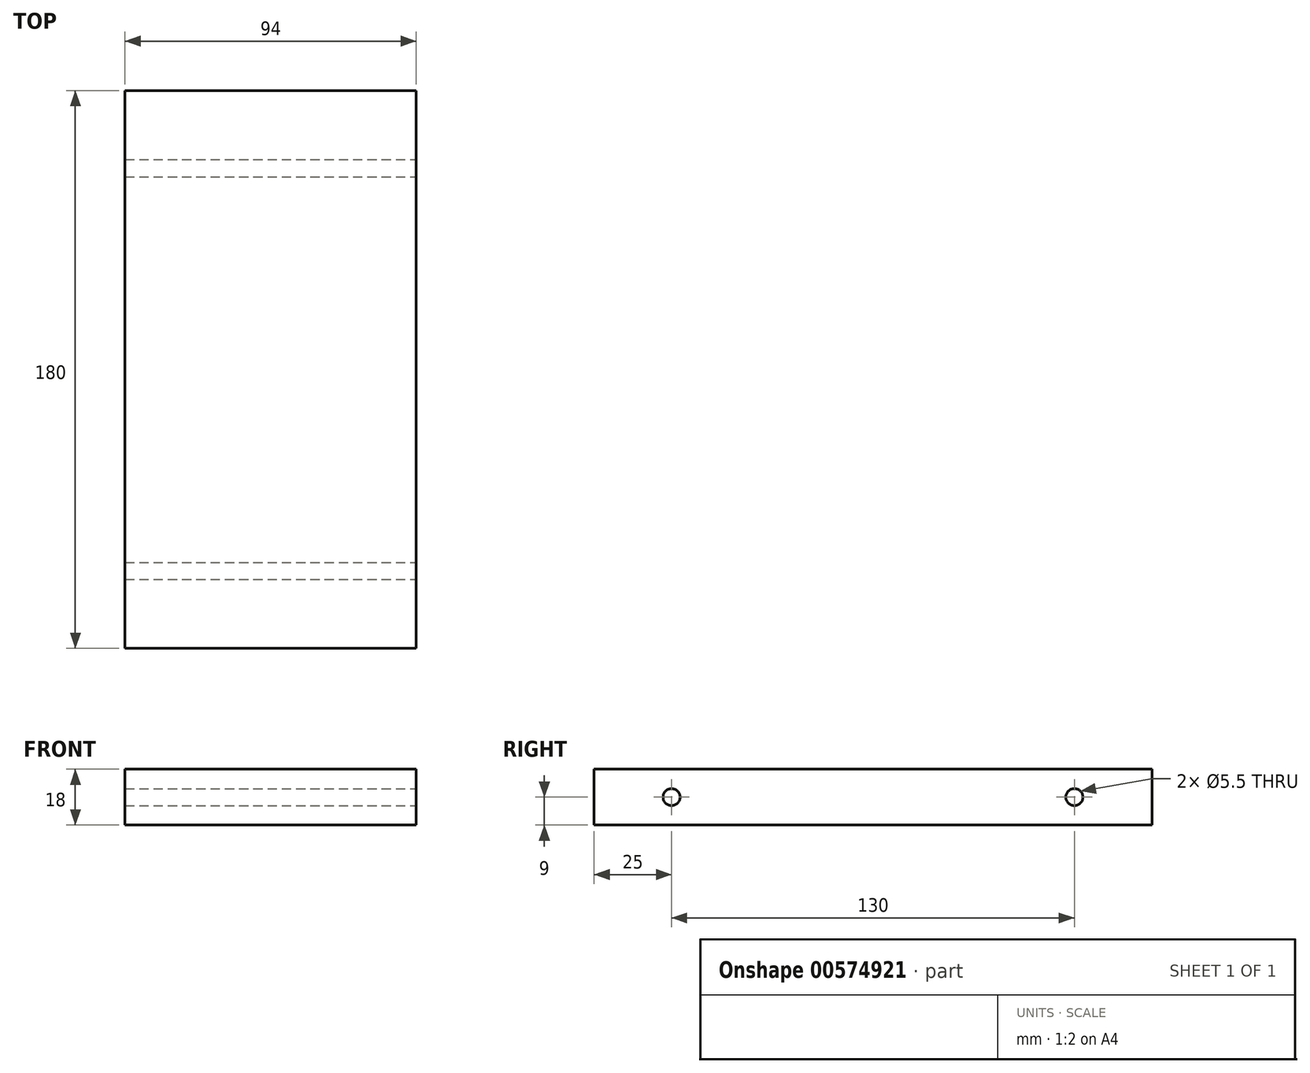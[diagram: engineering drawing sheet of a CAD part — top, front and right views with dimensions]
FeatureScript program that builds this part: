
annotation { "Feature Type Name" : "Feature", "Feature Type Description" : "" }
export const myFeature = defineFeature(function(context is Context, id is Id, definition is map)
    precondition{}
    {
        {
            var Q0;
            Q0=qCreatedBy(makeId("Front.planeOp"),FACE);
            var sketch = newSketch(context, id + "F0", { "sketchPlane" : qUnion([Q0])});
            skLineSegment(sketch, "E0.bottom", {"start": v(47, 9) * mm, "end": v(-47, 9) * mm});
            skLineSegment(sketch, "E0.top", {"start": v(47, -9) * mm, "end": v(-47, -9) * mm});
            skLineSegment(sketch, "E0.left", {"start": v(47, 9) * mm, "end": v(47, -9) * mm});
            skLineSegment(sketch, "E0.right", {"start": v(-47, 9) * mm, "end": v(-47, -9) * mm});
            skPoint(sketch, "E0.middle", {"position": v(0, 0) * mm});
            skSolve(sketch);
        }
        {
            var Q0;
            Q0=makeQuery(id+"F0.imprint","IMPRINT",FACE,{"disambiguationData":[TD([[makeQuery(id+"F0.imprint","IMPRINT",EDGE,{"derivedFrom":sQuery(id+"F0.wireOp",EDGE,"E0.bottom")}),1.0]])]});
            extrude(context, id + "F1", {"entities" : qUnion([Q0]), "depth" : 180 * mm, "offsetDistance" : 25 * mm, "symmetric" : true});
        }
        {
            var Q0;
            Q0=makeQuery(id+"F1.opExtrude","SWEPT_FACE",FACE,{"disambiguationData":[OSD([sQuery(id+"F0.wireOp",EDGE,"E0.left")])]});
            var sketch = newSketch(context, id + "F2", { "sketchPlane" : qUnion([Q0])});
            skPoint(sketch, "E1", {"position": v(-65, 0) * mm});
            skPoint(sketch, "E2", {"position": v(65, 0) * mm});
            skSolve(sketch);
        }
        {
            var Q0;
            Q0=sQuery(id+"F2.wireOp",VERTEX,"E1");
            var Q1;
            Q1=sQuery(id+"F2.wireOp",VERTEX,"E2");
            var Q2;
            Q2=makeQuery(id+"F1.opExtrude","SWEPT_BODY",BODY,{"disambiguationData":[OSD([sQuery(id+"F0.wireOp",EDGE,"E0.bottom"),sQuery(id+"F0.wireOp",EDGE,"E0.top"),sQuery(id+"F0.wireOp",EDGE,"E0.left"),sQuery(id+"F0.wireOp",EDGE,"E0.right")])]});
            hole(context, id + "F3", {"style" : HoleStyle.SIMPLE, "endStyle" : HoleEndStyle.THROUGH, "holeDiameter" : 5.5 * mm, "majorDiameter" : 5 * mm, "isTappedThrough" : true, "tappedDepth" : 12 * mm, "tapClearance" : 3, "locations" : qUnion([Q0, Q1]), "scope" : qUnion([Q2])});
        }
    });
